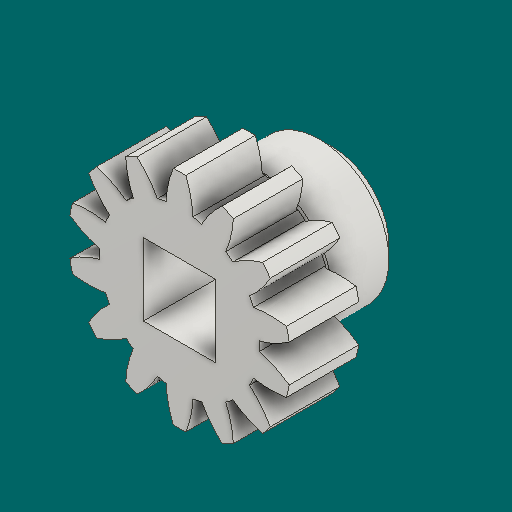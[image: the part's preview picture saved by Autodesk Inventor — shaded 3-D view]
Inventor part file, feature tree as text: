
AUTODESK INVENTOR PART (.ipt)
format: ipt  version: 2023.1 (Build 271208000, 208)  size: 317,952 bytes
history: native  units: in
note: dims shown in document units (in); Inventor stores cm internally (conversion verified against a paired STEP export)
features: other x12, sketch x5, plane x4
ambient origin geometry x8: Origin, YZ Plane, XZ Plane, XY Plane, X Axis, Y Axis, Z Axis, Center Point
bodies: Solid1 (feature_tree)
feature tree (21):
  other  "Spur Gear1"
  other  "Solid1::Spur Gear1"
  other  "TaggingFeature1"
  sketch  "Sketch1"  dims[d0=0.3937in]
  sketch  "Sketch2"  dims[d9=0.0in]
  sketch  "Sketch3"  dims[d14=0.0in]
  sketch  "Sketch4"  dims[d15=0.7in]
  sketch  "Sketch5"  dims[d16=0.0in d17=0.0in d18=0.0in d19=0.7in]
  plane  "XZ Plane_1"
  plane  "Work Plane2"
  plane  "Work Plane3"
  plane  "Work Plane4"
  other  "Srf1"
  other  "Srf1::Derived"
  other  "Start plane iMate"
  other  "Distance iMate"
  other  "Position iMate"
  other  "Mesh iMate"
  other  "Axis iMate"
  other  "Mesh iMate2"
  other  "Align iMate"
